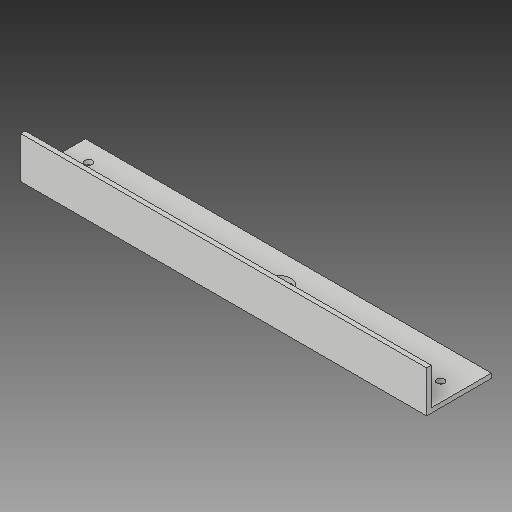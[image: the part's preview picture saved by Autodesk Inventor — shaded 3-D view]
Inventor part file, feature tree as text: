
AUTODESK INVENTOR PART (.ipt)
format: ipt  version: 2018 (Build 220112000, 112)  size: 103,424 bytes
history: native  units: in
note: dims shown in document units (in); Inventor stores cm internally (conversion verified against a paired STEP export)
features: sketch x4, other x3
ambient origin geometry x8: Origin, YZ Plane, XZ Plane, XY Plane, X Axis, Y Axis, Z Axis, Center Point
bodies: Solid1 (feature_tree)
feature tree (7):
  other  "angle iron with  holes 2_MIR.ipt"
  other  "Solid1::angle iron with  holes 2_MIR.ipt"
  other  "TaggingFeature1"
  sketch  "Sketch1"  dims[d0=0.3937in]
  sketch  "Sketch2"
  sketch  "Sketch3"
  sketch  "Sketch4"
